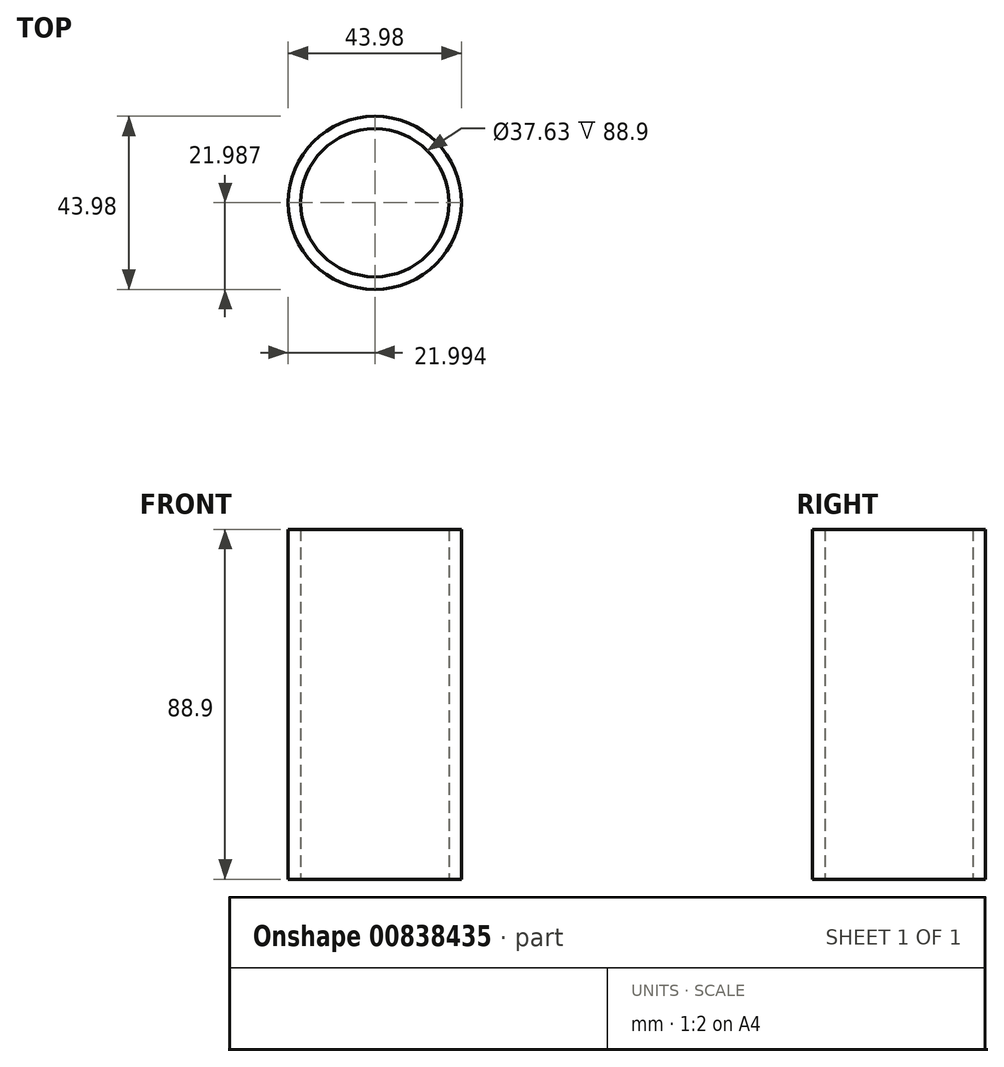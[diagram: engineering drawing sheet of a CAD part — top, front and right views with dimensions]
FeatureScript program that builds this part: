
annotation { "Feature Type Name" : "Feature", "Feature Type Description" : "" }
export const myFeature = defineFeature(function(context is Context, id is Id, definition is map)
    precondition{}
    {
        {
            var Q0;
            Q0=qCreatedBy(makeId("Top.planeOp"),FACE);
            var sketch = newSketch(context, id + "F0", { "sketchPlane" : qUnion([Q0])});
            skCircle(sketch, "E0", {"center": v(97.61, -210.01) * mm, "radius": 18.81 * mm});
            skCircle(sketch, "E1.0", {"center": v(97.61, -210.01) * mm, "radius": 21.99 * mm});
            skLineSegment(sketch, "E2", {"start": v(97.61, -210.01) * mm, "end": v(109.1, -224.92) * mm});
            skSolve(sketch);
        }
        {
            var Q0;
            Q0=makeQuery(id+"F0.imprint","IMPRINT",FACE,{"disambiguationData":[TD([[makeQuery(id+"F0.imprint","IMPRINT",EDGE,{"derivedFrom":sQuery(id+"F0.wireOp",EDGE,"E0")}),-1.0]])]});
            extrude(context, id + "F1", {"entities" : qUnion([Q0]), "depth" : 88.9 * mm, "offsetDistance" : 25.4 * mm});
        }
    });
